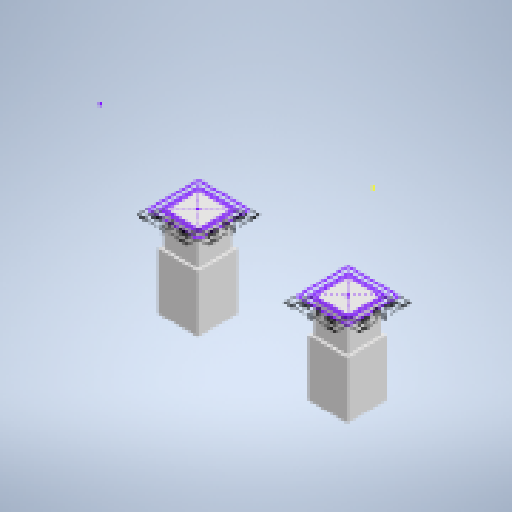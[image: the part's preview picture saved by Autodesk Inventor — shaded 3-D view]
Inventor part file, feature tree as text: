
AUTODESK INVENTOR PART (.ipt)
format: ipt  version: 2024 (Build 280153000, 153)  size: 164,864 bytes
history: native  units: mm
features: sketch x2, extrude x2
ambient origin geometry x8: Origin, YZ Plane, XZ Plane, XY Plane, X Axis, Y Axis, Z Axis, Center Point
bodies: Volumenkörper1 (feature_tree)
feature tree (4):
  sketch  "Skizze1"  dims[d0=7.0mm d1=7.0mm d2=9.0mm d3=9.0mm d4=6.0mm d5=6.0mm d6=6.0mm d7=6.0mm d8=7.0mm d9=7.0mm d10=9.0mm d11=9.0mm d12=6.0mm d13=0.0mm]
  extrude  "Extrusion1"  Depth=6.0mm TaperAngle=0.0deg
  extrude  "Extrusion2"  Depth=9.5mm
  sketch  "Skizze2"  dims[d15=3.0mm d16=3.0mm d17=3.0mm d18=7.0mm d19=7.0mm d20=7.0mm d21=7.0mm d22=9.5mm d23=0.0mm]
